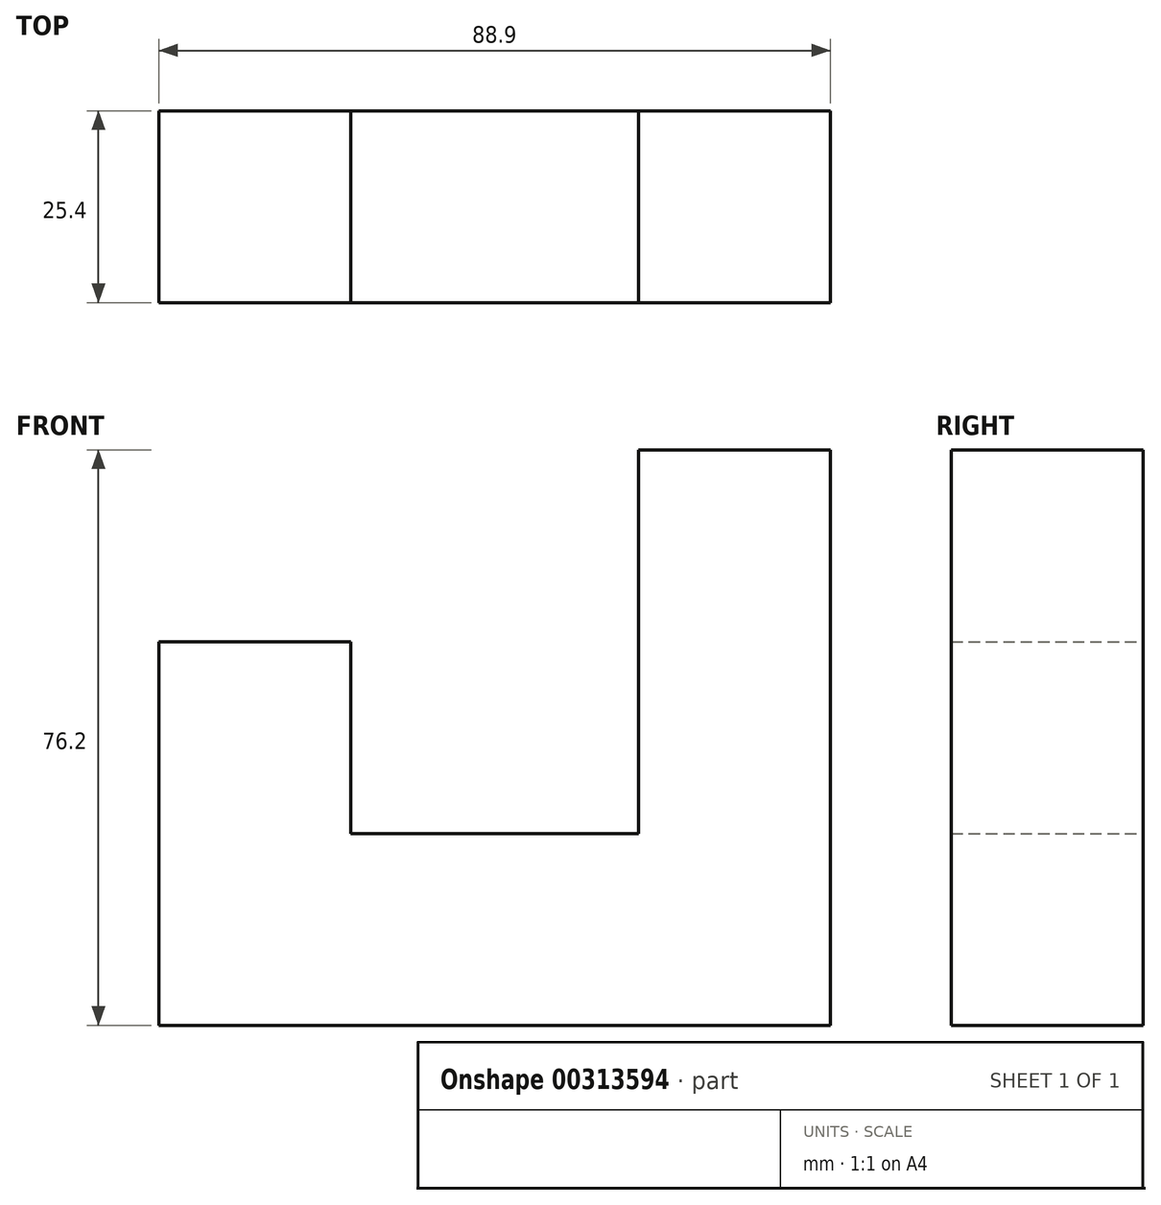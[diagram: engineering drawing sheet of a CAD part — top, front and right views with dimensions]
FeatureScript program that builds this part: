
annotation { "Feature Type Name" : "Feature", "Feature Type Description" : "" }
export const myFeature = defineFeature(function(context is Context, id is Id, definition is map)
    precondition{}
    {
        {
            var Q0;
            Q0=qCreatedBy(makeId("Front.planeOp"),FACE);
            var sketch = newSketch(context, id + "F0", { "sketchPlane" : qUnion([Q0])});
            skLineSegment(sketch, "E0", {"start": v(-37.36, -48.31) * mm, "end": v(51.54, -48.31) * mm});
            skLineSegment(sketch, "E1", {"start": v(51.54, -48.31) * mm, "end": v(51.54, 27.89) * mm});
            skLineSegment(sketch, "E2", {"start": v(51.54, 27.89) * mm, "end": v(26.14, 27.89) * mm});
            skLineSegment(sketch, "E3", {"start": v(26.14, 27.89) * mm, "end": v(26.14, -22.91) * mm});
            skLineSegment(sketch, "E4", {"start": v(26.14, -22.91) * mm, "end": v(-11.96, -22.91) * mm});
            skLineSegment(sketch, "E5", {"start": v(-11.96, -22.91) * mm, "end": v(-11.96, 2.49) * mm});
            skLineSegment(sketch, "E6", {"start": v(-11.96, 2.49) * mm, "end": v(-37.36, 2.49) * mm});
            skLineSegment(sketch, "E7", {"start": v(-37.36, 2.49) * mm, "end": v(-37.36, -48.31) * mm});
            skSolve(sketch);
        }
        {
            var Q0;
            Q0=makeQuery(id+"F0.imprint","IMPRINT",FACE,{"disambiguationData":[TD([[makeQuery(id+"F0.imprint","IMPRINT",EDGE,{"derivedFrom":sQuery(id+"F0.wireOp",EDGE,"E0")}),1.0]])]});
            extrude(context, id + "F1", {"entities" : qUnion([Q0]), "depth" : 25.4 * mm});
        }
    });
